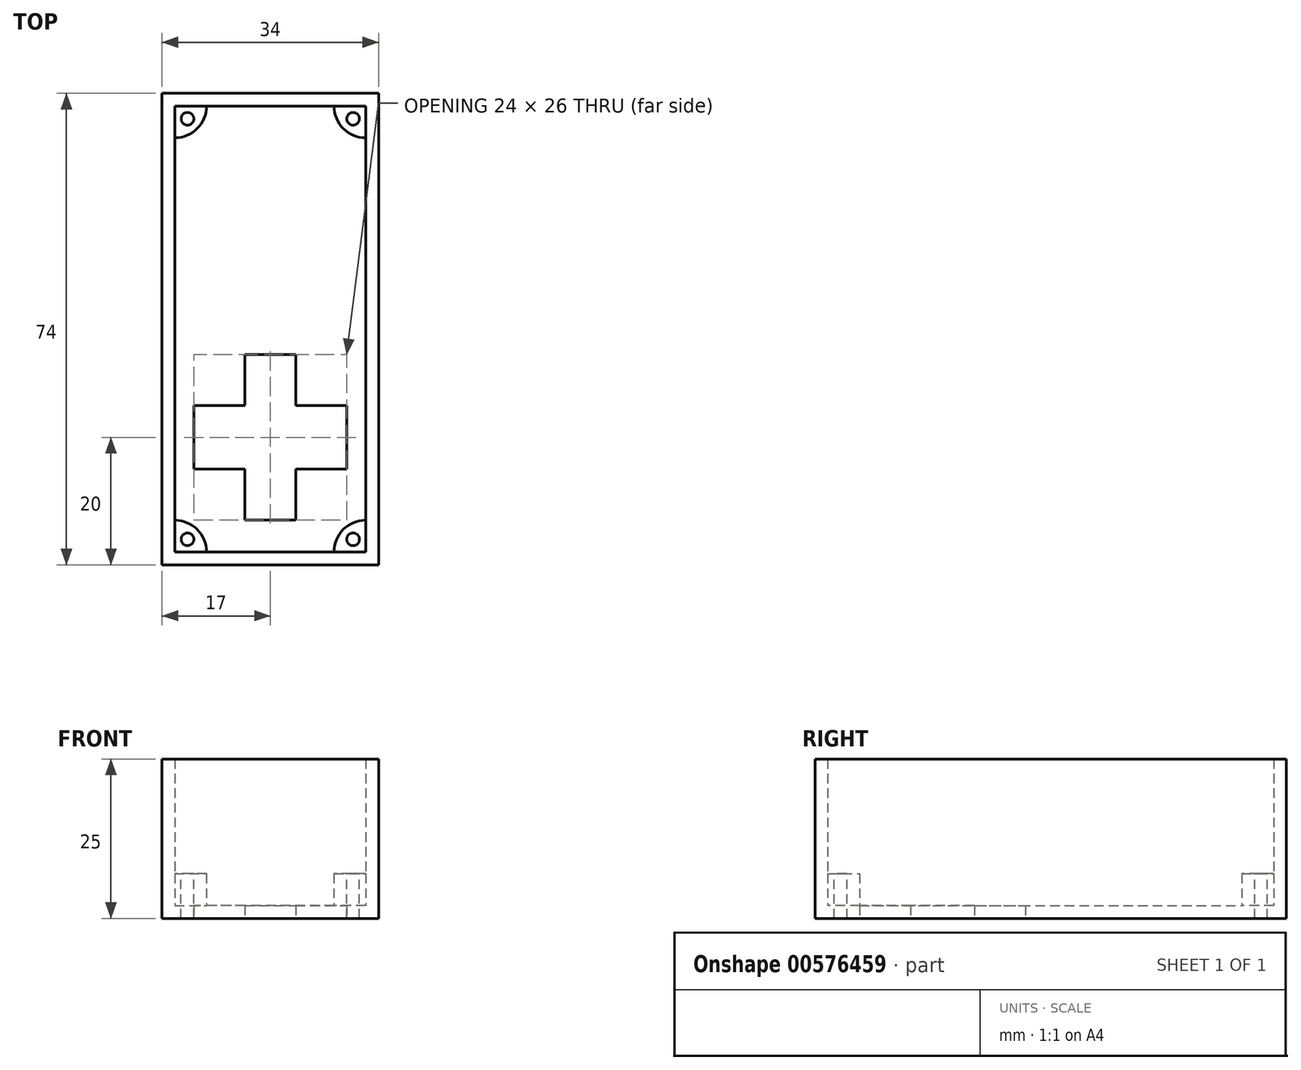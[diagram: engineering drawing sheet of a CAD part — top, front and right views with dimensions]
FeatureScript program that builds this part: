
annotation { "Feature Type Name" : "Feature", "Feature Type Description" : "" }
export const myFeature = defineFeature(function(context is Context, id is Id, definition is map)
    precondition{}
    {
        {
            var Q0;
            Q0=qCreatedBy(makeId("Top.planeOp"),FACE);
            var sketch = newSketch(context, id + "F0", { "sketchPlane" : qUnion([Q0])});
            skPoint(sketch, "E0.middle", {"position": v(0, 0) * mm});
            skLineSegment(sketch, "E1.0", {"start": v(17, 37) * mm, "end": v(-17, 37) * mm});
            skLineSegment(sketch, "E1.1", {"start": v(17, -37) * mm, "end": v(17, 37) * mm});
            skLineSegment(sketch, "E1.2", {"start": v(17, -37) * mm, "end": v(-17, -37) * mm});
            skLineSegment(sketch, "E1.3", {"start": v(-17, -37) * mm, "end": v(-17, 37) * mm});
            skSolve(sketch);
        }
        {
            var Q0;
            Q0 = qSketchRegion(id + "F0", true);
            extrude(context, id + "F1", {"entities" : qUnion([Q0]), "depth" : 25 * mm, "offsetDistance" : 25 * mm});
        }
        {
            var Q0;
            Q0=makeQuery(id+"F1.opExtrude","CAP_FACE",FACE,{"disambiguationData":[OSD([sQuery(id+"F0.wireOp",EDGE,"E1.0"),sQuery(id+"F0.wireOp",EDGE,"E1.1"),sQuery(id+"F0.wireOp",EDGE,"E1.2"),sQuery(id+"F0.wireOp",EDGE,"E1.3")])],"isStart":false});
            shell(context, id + "F2", {"entities" : qUnion([Q0]), "thickness" : 2 * mm});
        }
        {
            var Q0;
            Q0=makeQuery(id+"F2.opShell","OFFSET_FACE",FACE,{"disambiguationData":[OSD([sQuery(id+"F0.wireOp",EDGE,"E1.0"),sQuery(id+"F0.wireOp",EDGE,"E1.1"),sQuery(id+"F0.wireOp",EDGE,"E1.2"),sQuery(id+"F0.wireOp",EDGE,"E1.3")])]});
            var sketch = newSketch(context, id + "F3", { "sketchPlane" : qUnion([Q0])});
            skLineSegment(sketch, "E2.0", {"start": v(-13, -33) * mm, "end": v(-13, 33) * mm, "construction": true});
            skLineSegment(sketch, "E2.1", {"start": v(13, -33) * mm, "end": v(-13, -33) * mm, "construction": true});
            skLineSegment(sketch, "E2.2", {"start": v(13, -33) * mm, "end": v(13, 33) * mm, "construction": true});
            skLineSegment(sketch, "E2.3", {"start": v(13, 33) * mm, "end": v(-13, 33) * mm, "construction": true});
            skCircle(sketch, "E3", {"center": v(-13, -33) * mm, "radius": 1 * mm});
            skCircle(sketch, "E4", {"center": v(13, -33) * mm, "radius": 1 * mm});
            skCircle(sketch, "E5", {"center": v(-13, 33) * mm, "radius": 1 * mm});
            skCircle(sketch, "E6", {"center": v(13, 33) * mm, "radius": 1 * mm});
            skSolve(sketch);
        }
        {
            var Q0;
            Q0=makeQuery(id+"F3.imprint","IMPRINT",FACE,{"disambiguationData":[TD([[makeQuery(id+"F3.imprint","IMPRINT",EDGE,{"derivedFrom":sQuery(id+"F3.wireOp",EDGE,"E6")}),1.0]])]});
            var Q1;
            Q1=makeQuery(id+"F3.imprint","IMPRINT",FACE,{"disambiguationData":[TD([[makeQuery(id+"F3.imprint","IMPRINT",EDGE,{"derivedFrom":sQuery(id+"F3.wireOp",EDGE,"E5")}),1.0]])]});
            var Q2;
            Q2=makeQuery(id+"F3.imprint","IMPRINT",FACE,{"disambiguationData":[TD([[makeQuery(id+"F3.imprint","IMPRINT",EDGE,{"derivedFrom":sQuery(id+"F3.wireOp",EDGE,"E4")}),1.0]])]});
            var Q3;
            Q3=makeQuery(id+"F3.imprint","IMPRINT",FACE,{"disambiguationData":[TD([[makeQuery(id+"F3.imprint","IMPRINT",EDGE,{"derivedFrom":sQuery(id+"F3.wireOp",EDGE,"E3")}),1.0]])]});
            var Q4;
            Q4=sQuery(id+"F3.wireOp",EDGE,"E6");
            extrude(context, id + "F4", {"entities" : qUnion([Q0, Q1, Q2, Q3]), "operationType" : NewBodyOperationType.REMOVE, "surfaceEntities" : qUnion([Q4]), "oppositeDirection" : true, "depth" : 25 * mm, "offsetDistance" : 25 * mm});
        }
        {
            var Q0;
            Q0=makeQuery(id+"F2.opShell","OFFSET_FACE",FACE,{"disambiguationData":[OSD([sQuery(id+"F0.wireOp",EDGE,"E1.0"),sQuery(id+"F0.wireOp",EDGE,"E1.1"),sQuery(id+"F0.wireOp",EDGE,"E1.2"),sQuery(id+"F0.wireOp",EDGE,"E1.3")])]});
            var sketch = newSketch(context, id + "F5", { "sketchPlane" : qUnion([Q0])});
            skLineSegment(sketch, "E7.bottom", {"start": v(-15, -35) * mm, "end": v(-10, -35) * mm, "construction": true});
            skLineSegment(sketch, "E7.top", {"start": v(-15, -30) * mm, "end": v(-10, -30) * mm, "construction": true});
            skLineSegment(sketch, "E7.left", {"start": v(-15, -35) * mm, "end": v(-15, -30) * mm, "construction": true});
            skLineSegment(sketch, "E7.right", {"start": v(-10, -35) * mm, "end": v(-10, -30) * mm, "construction": true});
            skLineSegment(sketch, "E8.bottom", {"start": v(15, -35) * mm, "end": v(10, -35) * mm, "construction": true});
            skLineSegment(sketch, "E8.top", {"start": v(15, -30) * mm, "end": v(10, -30) * mm, "construction": true});
            skLineSegment(sketch, "E8.left", {"start": v(15, -35) * mm, "end": v(15, -30) * mm, "construction": true});
            skLineSegment(sketch, "E8.right", {"start": v(10, -35) * mm, "end": v(10, -30) * mm, "construction": true});
            skLineSegment(sketch, "E9.bottom", {"start": v(-15, 35) * mm, "end": v(-10, 35) * mm, "construction": true});
            skLineSegment(sketch, "E9.top", {"start": v(-15, 30) * mm, "end": v(-10, 30) * mm, "construction": true});
            skLineSegment(sketch, "E9.left", {"start": v(-15, 35) * mm, "end": v(-15, 30) * mm, "construction": true});
            skLineSegment(sketch, "E9.right", {"start": v(-10, 35) * mm, "end": v(-10, 30) * mm, "construction": true});
            skLineSegment(sketch, "E10.bottom", {"start": v(15, 35) * mm, "end": v(10, 35) * mm, "construction": true});
            skLineSegment(sketch, "E10.top", {"start": v(15, 30) * mm, "end": v(10, 30) * mm, "construction": true});
            skLineSegment(sketch, "E10.left", {"start": v(15, 35) * mm, "end": v(15, 30) * mm, "construction": true});
            skLineSegment(sketch, "E10.right", {"start": v(10, 35) * mm, "end": v(10, 30) * mm, "construction": true});
            skArc(sketch, "E11", {"start": v(10, 35) * mm, "mid": v(11.46, 31.46) * mm, "end": v(15, 30) * mm});
            skArc(sketch, "E12", {"start": v(-15, 30) * mm, "mid": v(-11.46, 31.46) * mm, "end": v(-10, 35) * mm});
            skArc(sketch, "E13", {"start": v(-10, -35) * mm, "mid": v(-11.46, -31.46) * mm, "end": v(-15, -30) * mm});
            skArc(sketch, "E14", {"start": v(15, -30) * mm, "mid": v(11.46, -31.46) * mm, "end": v(10, -35) * mm});
            skSolve(sketch);
        }
        {
            var Q0;
            {var subQ0=sQuery(id+"F5.wireOp",EDGE,"E14");Q0=makeQuery(id+"F5.imprint","IMPRINT",FACE,{"disambiguationData":[TD([[makeQuery(id+"F5.imprint","IMPRINT",EDGE,{"derivedFrom":subQ0}),1.0]])]});}
            var Q1;
            {var subQ0=sQuery(id+"F5.wireOp",EDGE,"E13");Q1=makeQuery(id+"F5.imprint","IMPRINT",FACE,{"disambiguationData":[TD([[makeQuery(id+"F5.imprint","IMPRINT",EDGE,{"derivedFrom":subQ0}),1.0]])]});}
            var Q2;
            {var subQ0=sQuery(id+"F5.wireOp",EDGE,"E12");Q2=makeQuery(id+"F5.imprint","IMPRINT",FACE,{"disambiguationData":[TD([[makeQuery(id+"F5.imprint","IMPRINT",EDGE,{"derivedFrom":subQ0}),1.0]])]});}
            var Q3;
            {var subQ0=sQuery(id+"F5.wireOp",EDGE,"E11");Q3=makeQuery(id+"F5.imprint","IMPRINT",FACE,{"disambiguationData":[TD([[makeQuery(id+"F5.imprint","IMPRINT",EDGE,{"derivedFrom":subQ0}),1.0]])]});}
            extrude(context, id + "F6", {"entities" : qUnion([Q0, Q1, Q2, Q3]), "operationType" : NewBodyOperationType.ADD, "depth" : 5 * mm, "offsetDistance" : 25 * mm});
        }
        {
            var Q0;
            Q0=makeQuery(id+"F1.opExtrude","CAP_FACE",FACE,{"disambiguationData":[OSD([sQuery(id+"F0.wireOp",EDGE,"E1.0"),sQuery(id+"F0.wireOp",EDGE,"E1.1"),sQuery(id+"F0.wireOp",EDGE,"E1.2"),sQuery(id+"F0.wireOp",EDGE,"E1.3")])],"isStart":true});
            var sketch = newSketch(context, id + "F7", { "sketchPlane" : qUnion([Q0])});
            skLineSegment(sketch, "E15.0", {"start": v(17, 30) * mm, "end": v(-17, 30) * mm});
            skLineSegment(sketch, "E16.0", {"start": v(12, 37) * mm, "end": v(12, -37) * mm});
            skLineSegment(sketch, "E17.0", {"start": v(-12, 37) * mm, "end": v(-12, -37) * mm});
            skLineSegment(sketch, "E18.0", {"start": v(17, 4) * mm, "end": v(-17, 4) * mm});
            skLineSegment(sketch, "E19.bottom", {"start": v(12, 4) * mm, "end": v(4, 4) * mm, "construction": true});
            skLineSegment(sketch, "E19.top", {"start": v(12, 12) * mm, "end": v(4, 12) * mm});
            skLineSegment(sketch, "E19.left", {"start": v(12, 4) * mm, "end": v(12, 12) * mm, "construction": true});
            skLineSegment(sketch, "E19.right", {"start": v(4, 4) * mm, "end": v(4, 12) * mm});
            skLineSegment(sketch, "E20.bottom", {"start": v(-12, 4) * mm, "end": v(-4, 4) * mm, "construction": true});
            skLineSegment(sketch, "E20.top", {"start": v(-12, 12) * mm, "end": v(-4, 12) * mm});
            skLineSegment(sketch, "E20.left", {"start": v(-12, 4) * mm, "end": v(-12, 12) * mm, "construction": true});
            skLineSegment(sketch, "E20.right", {"start": v(-4, 4) * mm, "end": v(-4, 12) * mm});
            skLineSegment(sketch, "E21.bottom", {"start": v(-12, 30) * mm, "end": v(-4, 30) * mm, "construction": true});
            skLineSegment(sketch, "E21.top", {"start": v(-12, 22) * mm, "end": v(-4, 22) * mm});
            skLineSegment(sketch, "E21.left", {"start": v(-12, 30) * mm, "end": v(-12, 22) * mm, "construction": true});
            skLineSegment(sketch, "E21.right", {"start": v(-4, 30) * mm, "end": v(-4, 22) * mm});
            skLineSegment(sketch, "E22.bottom", {"start": v(12, 30) * mm, "end": v(4, 30) * mm, "construction": true});
            skLineSegment(sketch, "E22.top", {"start": v(12, 22) * mm, "end": v(4, 22) * mm});
            skLineSegment(sketch, "E22.left", {"start": v(12, 30) * mm, "end": v(12, 22) * mm, "construction": true});
            skLineSegment(sketch, "E22.right", {"start": v(4, 30) * mm, "end": v(4, 22) * mm});
            skSolve(sketch);
        }
        {
            var Q0;
            {var subQ6=sQuery(id+"F7.wireOp",EDGE,"E19.top");Q0=makeQuery(id+"F7.imprint","IMPRINT",FACE,{"disambiguationData":[TD([[makeQuery(id+"F7.imprint","IMPRINT",EDGE,{"derivedFrom":subQ6}),-1.0]])]});}
            extrude(context, id + "F8", {"entities" : qUnion([Q0]), "operationType" : NewBodyOperationType.REMOVE, "oppositeDirection" : true, "depth" : 25 * mm, "offsetDistance" : 25 * mm});
        }
    });
